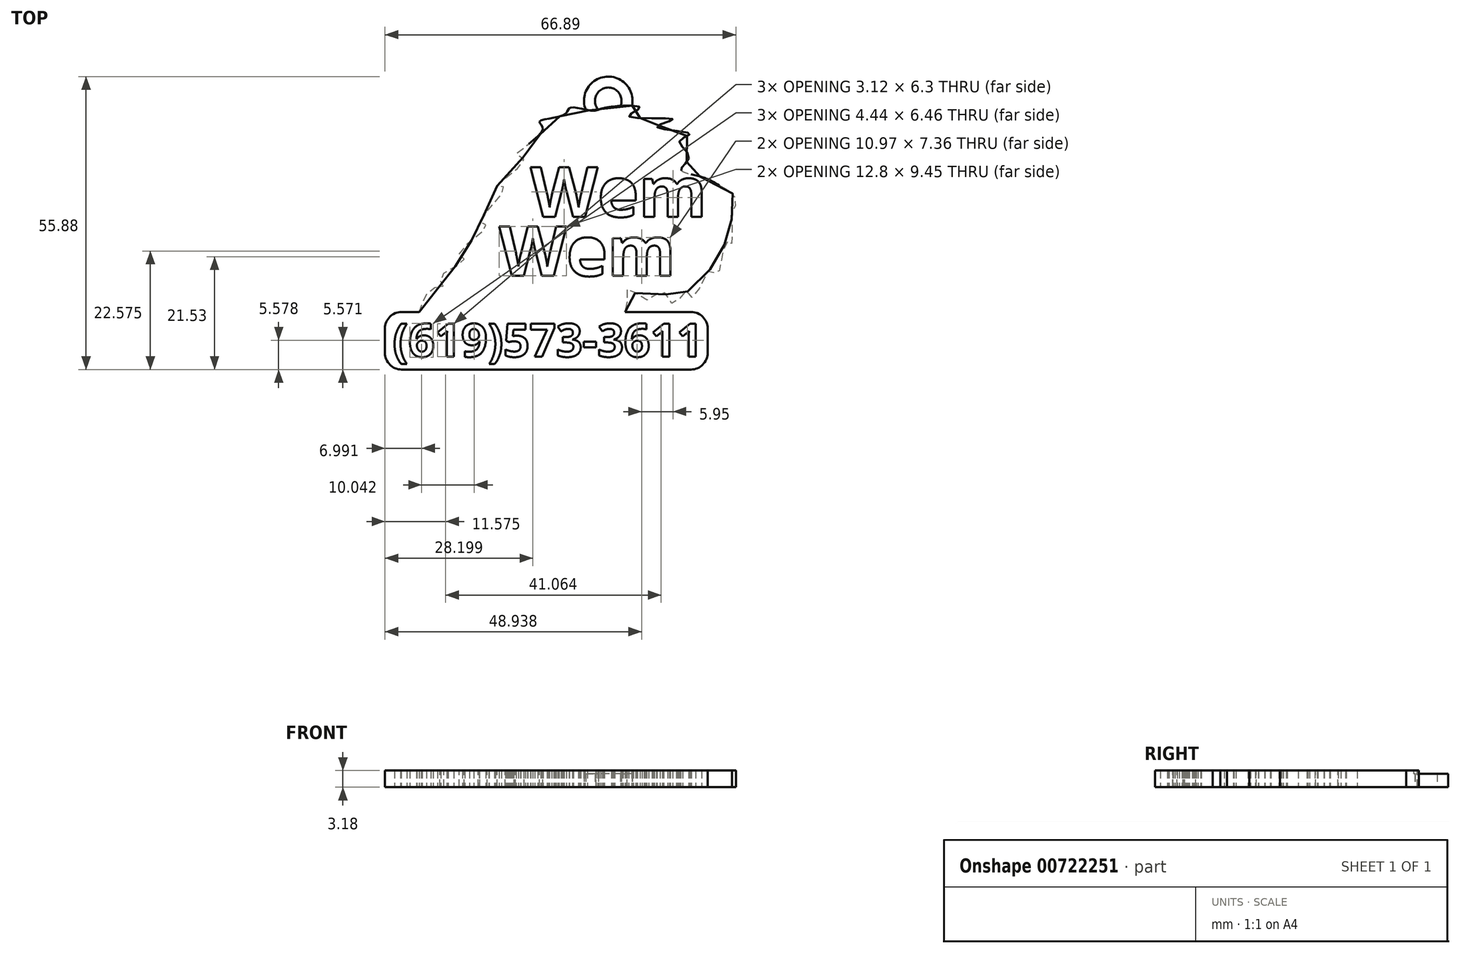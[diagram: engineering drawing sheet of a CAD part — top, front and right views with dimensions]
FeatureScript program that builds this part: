
annotation { "Feature Type Name" : "Feature", "Feature Type Description" : "" }
export const myFeature = defineFeature(function(context is Context, id is Id, definition is map)
    precondition{}
    {
        {
            var Q0;
            Q0=qCreatedBy(makeId("Top.planeOp"),FACE);
            var sketch = newSketch(context, id + "F0", { "sketchPlane" : qUnion([Q0])});
            skFitSpline(sketch, "E0", {"points": [v(-24.49, -20.7) * mm, v(-22.56, -18.02) * mm, v(-20.5, -17.54) * mm, v(-21.2, -15.97) * mm, v(-16.56, -12.63) * mm, v(-17.56, -11.55) * mm, v(-12.2, -6.08) * mm, v(-13.6, -5.54) * mm, v(-8.82, 1.12) * mm, v(-10.3, 1.38) * mm, v(-6.09, 5.16) * mm, v(-5.43, 7.01) * mm, v(-6.79, 7.4) * mm, v(-1.61, 12.25) * mm, v(-2.25, 13.75) * mm, v(2.64, 15.2) * mm, v(3.54, 16.38) * mm, v(7.74, 15.85) * mm, v(10.23, 16.38) * mm, v(16.93, 16.38) * mm, v(14.81, 14.77) * mm, v(23.17, 14.2) * mm, v(20.16, 12.8) * mm, v(26.46, 11.48) * mm, v(24.5, 10.12) * mm, v(26.23, 7.28) * mm, v(24.94, 5.09) * mm, v(24.8, 4.39) * mm, v(28.95, 3.12) * mm, v(32.96, 1.08) * mm, v(34.96, -0.47) * mm, v(35.02, -2.5) * mm, v(34.47, -3.6) * mm, v(34.28, -9.73) * mm, v(33.4, -9.05) * mm, v(31.67, -15.52) * mm, v(30.37, -14.42) * mm, v(27.02, -19.83) * mm, v(25.67, -18.44) * mm, v(23.4, -21.08) * mm, v(21.24, -18.58) * mm, v(18.51, -20.29) * mm, v(14.62, -18.06) * mm, v(14.46, -20.96) * mm, v(13.61, -23.98) * mm, v(12.2, -27.2) * mm, v(-23.22, -26.9) * mm, v(-25.48, -23.8) * mm, v(-24.49, -20.7) * mm]});
            skText(sketch, "E1", { "text": "Wem", "fontName": "OpenSans-Bold.ttf"});
            skText(sketch, "E2", { "text": "Wem", "fontName": "OpenSans-Bold.ttf"});
            const initialGuessF0  = {"E1": [-0.00395, -0.0044, 1, 0, 0.00953], "E2": [-0.0099, -0.01568, 1, 0, 0.00953]};
            skSetInitialGuess(sketch, initialGuessF0);
            skSolve(sketch);
        }
        {
            var Q0;
            Q0=makeQuery(id+"F0.imprint","IMPRINT",FACE,{"disambiguationData":[TD([[makeQuery(id+"F0.imprint","IMPRINT",EDGE,{"derivedFrom":sQuery(id+"F0.wireOp",EDGE,"E0")}),-1.0]])]});
            extrude(context, id + "F1", {"entities" : qUnion([Q0]), "depth" : 3.17 * mm, "offsetDistance" : 25.4 * mm});
        }
        {
            var Q0;
            Q0=qCreatedBy(makeId("Top.planeOp"),FACE);
            var sketch = newSketch(context, id + "F2", { "sketchPlane" : qUnion([Q0])});
            skText(sketch, "E3", { "text": "(619)573-3611", "fontName": "OpenSans-Bold.ttf"});
            const initialGuessF2  = {"E3": [-0.03023, -0.0311, 1, 0, 0.00635]};
            skSetInitialGuess(sketch, initialGuessF2);
            skSolve(sketch);
        }
        {
            var Q0;
            Q0=qCreatedBy(makeId("Top.planeOp"),FACE);
            var sketch = newSketch(context, id + "F3", { "sketchPlane" : qUnion([Q0])});
            skLineSegment(sketch, "E4.bottom", {"start": v(-31.7, -22.55) * mm, "end": v(29.81, -22.55) * mm});
            skLineSegment(sketch, "E4.top", {"start": v(-31.7, -33.53) * mm, "end": v(29.81, -33.53) * mm});
            skLineSegment(sketch, "E4.left", {"start": v(-31.7, -22.55) * mm, "end": v(-31.7, -33.53) * mm});
            skLineSegment(sketch, "E4.right", {"start": v(29.81, -22.55) * mm, "end": v(29.81, -33.53) * mm});
            skSolve(sketch);
        }
        {
            var Q0;
            Q0 = qSketchRegion(id + "F3", true);
            extrude(context, id + "F4", {"entities" : qUnion([Q0]), "operationType" : NewBodyOperationType.ADD, "depth" : 3.17 * mm, "offsetDistance" : 25.4 * mm});
        }
        {
            var Q0;
            Q0=makeQuery(id+"F4.opExtrude","SWEPT_EDGE",EDGE,{"disambiguationData":[OSD([sQuery(id+"F3.wireOp",EDGE,"E4.bottom"),sQuery(id+"F3.wireOp",EDGE,"E4.right")])]});
            var Q1;
            Q1=makeQuery(id+"F4.opExtrude","SWEPT_EDGE",EDGE,{"disambiguationData":[OSD([sQuery(id+"F3.wireOp",EDGE,"E4.top"),sQuery(id+"F3.wireOp",EDGE,"E4.right")])]});
            var Q2;
            Q2=makeQuery(id+"F4.opExtrude","SWEPT_EDGE",EDGE,{"disambiguationData":[OSD([sQuery(id+"F3.wireOp",EDGE,"E4.bottom"),sQuery(id+"F3.wireOp",EDGE,"E4.left")])]});
            var Q3;
            Q3=makeQuery(id+"F4.opExtrude","SWEPT_EDGE",EDGE,{"disambiguationData":[OSD([sQuery(id+"F3.wireOp",EDGE,"E4.top"),sQuery(id+"F3.wireOp",EDGE,"E4.left")])]});
            fillet(context, id + "F5", {"entities" : qUnion([Q0, Q1, Q2, Q3]), "radius" : 3.17 * mm, "tangentPropagation" : true, "allowEdgeOverflow" : false});
        }
        {
            var Q0;
            Q0 = qSketchRegion(id + "F2", true);
            extrude(context, id + "F6", {"entities" : qUnion([Q0]), "operationType" : NewBodyOperationType.REMOVE, "depth" : 5.08 * mm, "offsetDistance" : 25.4 * mm});
        }
        {
            var Q0;
            {var subQ0=sQuery(id+"F0.wireOp",EDGE,"E2.sketch_text.stroke-71");var subQ1=sQuery(id+"F0.wireOp",EDGE,"E2.sketch_text.stroke-70");var subQ2=sQuery(id+"F0.wireOp",EDGE,"E2.sketch_text.stroke-69");var subQ3=sQuery(id+"F0.wireOp",EDGE,"E2.sketch_text.stroke-68");var subQ4=sQuery(id+"F0.wireOp",EDGE,"E2.sketch_text.stroke-67");var subQ5=sQuery(id+"F0.wireOp",EDGE,"E2.sketch_text.stroke-66");var subQ6=sQuery(id+"F0.wireOp",EDGE,"E2.sketch_text.stroke-65");var subQ7=sQuery(id+"F0.wireOp",EDGE,"E2.sketch_text.stroke-64");var subQ8=sQuery(id+"F0.wireOp",EDGE,"E2.sketch_text.stroke-63");var subQ9=sQuery(id+"F0.wireOp",EDGE,"E2.sketch_text.stroke-62");var subQ10=sQuery(id+"F0.wireOp",EDGE,"E2.sketch_text.stroke-61");var subQ11=sQuery(id+"F0.wireOp",EDGE,"E2.sketch_text.stroke-60");var subQ12=sQuery(id+"F0.wireOp",EDGE,"E2.sketch_text.stroke-59");var subQ13=sQuery(id+"F0.wireOp",EDGE,"E2.sketch_text.stroke-58");var subQ14=sQuery(id+"F0.wireOp",EDGE,"E2.sketch_text.stroke-57");var subQ15=sQuery(id+"F0.wireOp",EDGE,"E2.sketch_text.stroke-56");var subQ16=sQuery(id+"F0.wireOp",EDGE,"E2.sketch_text.stroke-55");var subQ17=sQuery(id+"F0.wireOp",EDGE,"E2.sketch_text.stroke-54");var subQ18=sQuery(id+"F0.wireOp",EDGE,"E2.sketch_text.stroke-53");var subQ19=sQuery(id+"F0.wireOp",EDGE,"E2.sketch_text.stroke-52");var subQ20=sQuery(id+"F0.wireOp",EDGE,"E2.sketch_text.stroke-51");var subQ21=sQuery(id+"F0.wireOp",EDGE,"E2.sketch_text.stroke-50");var subQ22=sQuery(id+"F0.wireOp",EDGE,"E2.sketch_text.stroke-49");var subQ23=sQuery(id+"F0.wireOp",EDGE,"E2.sketch_text.stroke-48");var subQ24=sQuery(id+"F0.wireOp",EDGE,"E2.sketch_text.stroke-47");var subQ25=sQuery(id+"F0.wireOp",EDGE,"E2.sketch_text.stroke-46");var subQ26=sQuery(id+"F0.wireOp",EDGE,"E2.sketch_text.stroke-45");var subQ27=sQuery(id+"F0.wireOp",EDGE,"E2.sketch_text.stroke-44");var subQ28=sQuery(id+"F0.wireOp",EDGE,"E2.sketch_text.stroke-43");var subQ29=sQuery(id+"F0.wireOp",EDGE,"E2.sketch_text.stroke-42");var subQ30=sQuery(id+"F0.wireOp",EDGE,"E2.sketch_text.stroke-41");var subQ31=sQuery(id+"F0.wireOp",EDGE,"E2.sketch_text.stroke-40");var subQ32=sQuery(id+"F0.wireOp",EDGE,"E2.sketch_text.stroke-39");var subQ33=sQuery(id+"F0.wireOp",EDGE,"E2.sketch_text.stroke-38");var subQ34=sQuery(id+"F0.wireOp",EDGE,"E2.sketch_text.stroke-37");var subQ35=sQuery(id+"F0.wireOp",EDGE,"E2.sketch_text.stroke-36");var subQ36=sQuery(id+"F0.wireOp",EDGE,"E2.sketch_text.stroke-35");var subQ37=sQuery(id+"F0.wireOp",EDGE,"E2.sketch_text.stroke-34");var subQ38=sQuery(id+"F0.wireOp",EDGE,"E2.sketch_text.stroke-33");var subQ39=sQuery(id+"F0.wireOp",EDGE,"E1.sketch_text.stroke-48");var subQ40=sQuery(id+"F3.wireOp",EDGE,"E4.bottom");var subQ41=sQuery(id+"F0.wireOp",EDGE,"E1.sketch_text.stroke-47");var subQ42=sQuery(id+"F0.wireOp",EDGE,"E1.sketch_text.stroke-46");var subQ43=sQuery(id+"F0.wireOp",EDGE,"E1.sketch_text.stroke-45");var subQ44=sQuery(id+"F0.wireOp",EDGE,"E1.sketch_text.stroke-44");var subQ45=sQuery(id+"F0.wireOp",EDGE,"E1.sketch_text.stroke-43");var subQ46=sQuery(id+"F0.wireOp",EDGE,"E1.sketch_text.stroke-42");var subQ47=sQuery(id+"F0.wireOp",EDGE,"E1.sketch_text.stroke-41");var subQ48=sQuery(id+"F0.wireOp",EDGE,"E1.sketch_text.stroke-40");var subQ49=sQuery(id+"F0.wireOp",EDGE,"E1.sketch_text.stroke-39");var subQ50=sQuery(id+"F0.wireOp",EDGE,"E1.sketch_text.stroke-38");var subQ51=sQuery(id+"F0.wireOp",EDGE,"E1.sketch_text.stroke-37");var subQ52=sQuery(id+"F0.wireOp",EDGE,"E1.sketch_text.stroke-36");var subQ53=sQuery(id+"F0.wireOp",EDGE,"E1.sketch_text.stroke-35");var subQ54=sQuery(id+"F0.wireOp",EDGE,"E1.sketch_text.stroke-34");var subQ55=sQuery(id+"F0.wireOp",EDGE,"E1.sketch_text.stroke-33");var subQ56=sQuery(id+"F0.wireOp",EDGE,"E1.sketch_text.stroke-32");var subQ57=sQuery(id+"F0.wireOp",EDGE,"E1.sketch_text.stroke-31");var subQ58=sQuery(id+"F0.wireOp",EDGE,"E1.sketch_text.stroke-30");var subQ59=sQuery(id+"F0.wireOp",EDGE,"E1.sketch_text.stroke-29");var subQ60=sQuery(id+"F0.wireOp",EDGE,"E1.sketch_text.stroke-23");var subQ61=sQuery(id+"F0.wireOp",EDGE,"E1.sketch_text.stroke-22");var subQ62=sQuery(id+"F0.wireOp",EDGE,"E1.sketch_text.stroke-21");var subQ63=sQuery(id+"F0.wireOp",EDGE,"E1.sketch_text.stroke-7");var subQ64=sQuery(id+"F0.wireOp",EDGE,"E1.sketch_text.stroke-6");var subQ65=sQuery(id+"F0.wireOp",EDGE,"E1.sketch_text.stroke-5");var subQ66=sQuery(id+"F0.wireOp",EDGE,"E1.sketch_text.stroke-4");var subQ67=sQuery(id+"F0.wireOp",EDGE,"E1.sketch_text.stroke-3");var subQ68=sQuery(id+"F0.wireOp",EDGE,"E1.sketch_text.stroke-8");var subQ69=sQuery(id+"F0.wireOp",EDGE,"E1.sketch_text.stroke-49");var subQ70=sQuery(id+"F0.wireOp",EDGE,"E0");var subQ71=sQuery(id+"F0.wireOp",EDGE,"E2.sketch_text.stroke-32");var subQ72=sQuery(id+"F0.wireOp",EDGE,"E1.sketch_text.stroke-20");var subQ73=sQuery(id+"F0.wireOp",EDGE,"E1.sketch_text.stroke-2");var subQ74=sQuery(id+"F0.wireOp",EDGE,"E1.sketch_text.stroke-0");var subQ75=sQuery(id+"F0.wireOp",EDGE,"E1.sketch_text.stroke-1");var subQ76=sQuery(id+"F0.wireOp",EDGE,"E1.sketch_text.stroke-9");var subQ77=sQuery(id+"F0.wireOp",EDGE,"E1.sketch_text.stroke-10");var subQ78=sQuery(id+"F0.wireOp",EDGE,"E1.sketch_text.stroke-11");var subQ79=sQuery(id+"F0.wireOp",EDGE,"E1.sketch_text.stroke-12");var subQ80=sQuery(id+"F0.wireOp",EDGE,"E1.sketch_text.stroke-13");var subQ81=sQuery(id+"F0.wireOp",EDGE,"E1.sketch_text.stroke-14");var subQ82=sQuery(id+"F0.wireOp",EDGE,"E1.sketch_text.stroke-15");var subQ83=sQuery(id+"F0.wireOp",EDGE,"E1.sketch_text.stroke-16");var subQ84=sQuery(id+"F0.wireOp",EDGE,"E1.sketch_text.stroke-17");var subQ85=sQuery(id+"F0.wireOp",EDGE,"E1.sketch_text.stroke-18");var subQ86=sQuery(id+"F0.wireOp",EDGE,"E1.sketch_text.stroke-19");var subQ87=sQuery(id+"F3.wireOp",EDGE,"E4.top");var subQ88=sQuery(id+"F0.wireOp",EDGE,"E1.sketch_text.stroke-50");var subQ89=sQuery(id+"F3.wireOp",EDGE,"E4.left");var subQ90=sQuery(id+"F0.wireOp",EDGE,"E1.sketch_text.stroke-51");var subQ91=sQuery(id+"F3.wireOp",EDGE,"E4.right");var subQ92=sQuery(id+"F0.wireOp",EDGE,"E1.sketch_text.stroke-52");var subQ93=sQuery(id+"F0.wireOp",EDGE,"E1.sketch_text.stroke-53");var subQ94=sQuery(id+"F0.wireOp",EDGE,"E1.sketch_text.stroke-54");var subQ95=sQuery(id+"F0.wireOp",EDGE,"E1.sketch_text.stroke-55");var subQ96=sQuery(id+"F0.wireOp",EDGE,"E1.sketch_text.stroke-56");var subQ97=sQuery(id+"F0.wireOp",EDGE,"E1.sketch_text.stroke-57");var subQ98=sQuery(id+"F0.wireOp",EDGE,"E1.sketch_text.stroke-58");var subQ99=sQuery(id+"F0.wireOp",EDGE,"E1.sketch_text.stroke-59");var subQ100=sQuery(id+"F0.wireOp",EDGE,"E1.sketch_text.stroke-60");var subQ101=sQuery(id+"F0.wireOp",EDGE,"E1.sketch_text.stroke-61");var subQ102=sQuery(id+"F0.wireOp",EDGE,"E1.sketch_text.stroke-62");var subQ103=sQuery(id+"F0.wireOp",EDGE,"E1.sketch_text.stroke-63");var subQ104=sQuery(id+"F0.wireOp",EDGE,"E1.sketch_text.stroke-64");var subQ105=sQuery(id+"F0.wireOp",EDGE,"E1.sketch_text.stroke-65");var subQ106=sQuery(id+"F0.wireOp",EDGE,"E1.sketch_text.stroke-66");var subQ107=sQuery(id+"F0.wireOp",EDGE,"E1.sketch_text.stroke-67");var subQ108=sQuery(id+"F0.wireOp",EDGE,"E1.sketch_text.stroke-68");var subQ109=sQuery(id+"F0.wireOp",EDGE,"E1.sketch_text.stroke-69");var subQ110=sQuery(id+"F0.wireOp",EDGE,"E1.sketch_text.stroke-70");var subQ111=sQuery(id+"F0.wireOp",EDGE,"E1.sketch_text.stroke-71");var subQ112=sQuery(id+"F0.wireOp",EDGE,"E2.sketch_text.stroke-0");var subQ113=sQuery(id+"F0.wireOp",EDGE,"E2.sketch_text.stroke-1");var subQ114=sQuery(id+"F0.wireOp",EDGE,"E2.sketch_text.stroke-2");var subQ115=sQuery(id+"F0.wireOp",EDGE,"E2.sketch_text.stroke-3");var subQ116=sQuery(id+"F0.wireOp",EDGE,"E2.sketch_text.stroke-4");var subQ117=sQuery(id+"F0.wireOp",EDGE,"E2.sketch_text.stroke-5");var subQ118=sQuery(id+"F0.wireOp",EDGE,"E2.sketch_text.stroke-6");var subQ119=sQuery(id+"F0.wireOp",EDGE,"E2.sketch_text.stroke-7");var subQ120=sQuery(id+"F0.wireOp",EDGE,"E2.sketch_text.stroke-8");var subQ121=sQuery(id+"F0.wireOp",EDGE,"E2.sketch_text.stroke-9");var subQ122=sQuery(id+"F0.wireOp",EDGE,"E2.sketch_text.stroke-10");var subQ123=sQuery(id+"F0.wireOp",EDGE,"E2.sketch_text.stroke-11");var subQ124=sQuery(id+"F0.wireOp",EDGE,"E2.sketch_text.stroke-12");var subQ125=sQuery(id+"F0.wireOp",EDGE,"E2.sketch_text.stroke-13");var subQ126=sQuery(id+"F0.wireOp",EDGE,"E2.sketch_text.stroke-14");var subQ127=sQuery(id+"F0.wireOp",EDGE,"E2.sketch_text.stroke-15");var subQ128=sQuery(id+"F0.wireOp",EDGE,"E2.sketch_text.stroke-16");var subQ129=sQuery(id+"F0.wireOp",EDGE,"E2.sketch_text.stroke-17");var subQ130=sQuery(id+"F0.wireOp",EDGE,"E2.sketch_text.stroke-18");var subQ131=sQuery(id+"F0.wireOp",EDGE,"E2.sketch_text.stroke-19");var subQ132=sQuery(id+"F0.wireOp",EDGE,"E2.sketch_text.stroke-20");var subQ133=sQuery(id+"F0.wireOp",EDGE,"E2.sketch_text.stroke-21");var subQ134=sQuery(id+"F0.wireOp",EDGE,"E2.sketch_text.stroke-22");var subQ135=sQuery(id+"F0.wireOp",EDGE,"E2.sketch_text.stroke-23");var subQ136=sQuery(id+"F0.wireOp",EDGE,"E2.sketch_text.stroke-29");var subQ137=sQuery(id+"F0.wireOp",EDGE,"E2.sketch_text.stroke-30");var subQ138=sQuery(id+"F0.wireOp",EDGE,"E2.sketch_text.stroke-31");Q0=makeQuery(id+"F6.boolean.opBoolean","SPLIT",FACE,{"disambiguationData":[TD([makeQuery(id+"F1.opExtrude","SWEPT_FACE",FACE,{"disambiguationData":[OSD([subQ70])]})])],"derivedFrom":makeQuery(id+"F4.boolean.opBoolean","MERGE",FACE,{"derivedFrom":[makeQuery(id+"F1.opExtrude","CAP_FACE",FACE,{"disambiguationData":[OSD([subQ70,subQ74,subQ75,subQ73,subQ67,subQ66,subQ65,subQ64,subQ63,subQ68,subQ76,subQ77,subQ78,subQ79,subQ80,subQ81,subQ82,subQ83,subQ84,subQ85,subQ86,subQ72,subQ62,subQ61,subQ60,subQ59,subQ58,subQ57,subQ56,subQ55,subQ54,subQ53,subQ52,subQ51,subQ50,subQ49,subQ48,subQ47,subQ46,subQ45,subQ44,subQ43,subQ42,subQ41,subQ39,subQ69,subQ88,subQ90,subQ92,subQ93,subQ94,subQ95,subQ96,subQ97,subQ98,subQ99,subQ100,subQ101,subQ102,subQ103,subQ104,subQ105,subQ106,subQ107,subQ108,subQ109,subQ110,subQ111,subQ112,subQ113,subQ114,subQ115,subQ116,subQ117,subQ118,subQ119,subQ120,subQ121,subQ122,subQ123,subQ124,subQ125,subQ126,subQ127,subQ128,subQ129,subQ130,subQ131,subQ132,subQ133,subQ134,subQ135,subQ136,subQ137,subQ138,subQ71,subQ38,subQ37,subQ36,subQ35,subQ34,subQ33,subQ32,subQ31,subQ30,subQ29,subQ28,subQ27,subQ26,subQ25,subQ24,subQ23,subQ22,subQ21,subQ20,subQ19,subQ18,subQ17,subQ16,subQ15,subQ14,subQ13,subQ12,subQ11,subQ10,subQ9,subQ8,subQ7,subQ6,subQ5,subQ4,subQ3,subQ2,subQ1,subQ0])],"isStart":false}),makeQuery(id+"F4.opExtrude","CAP_FACE",FACE,{"disambiguationData":[OSD([subQ40,subQ87,subQ89,subQ91])],"isStart":false})]})});}
            cPlane(context, id + "F7", {"entities" : qUnion([Q0]), "cplaneType" : CPlaneType.OFFSET, "offset" : 1.59 * mm, "oppositeDirection" : true, "width" : 152.4 * mm, "height" : 152.4 * mm});
        }
        {
            var Q0;
            Q0=qCreatedBy(makeId("Top.planeOp"),FACE);
            var sketch = newSketch(context, id + "F8", { "sketchPlane" : qUnion([Q0])});
            skCircle(sketch, "E5", {"center": v(10.87, 17.72) * mm, "radius": 2.54 * mm});
            skCircle(sketch, "E6", {"center": v(10.87, 17.72) * mm, "radius": 4.62 * mm});
            skSolve(sketch);
        }
        {
            var Q0;
            Q0 = qSketchRegion(id + "F8", true);
            extrude(context, id + "F9", {"entities" : qUnion([Q0]), "operationType" : NewBodyOperationType.ADD, "depth" : 2.54 * mm, "offsetDistance" : 25.4 * mm});
        }
    });
